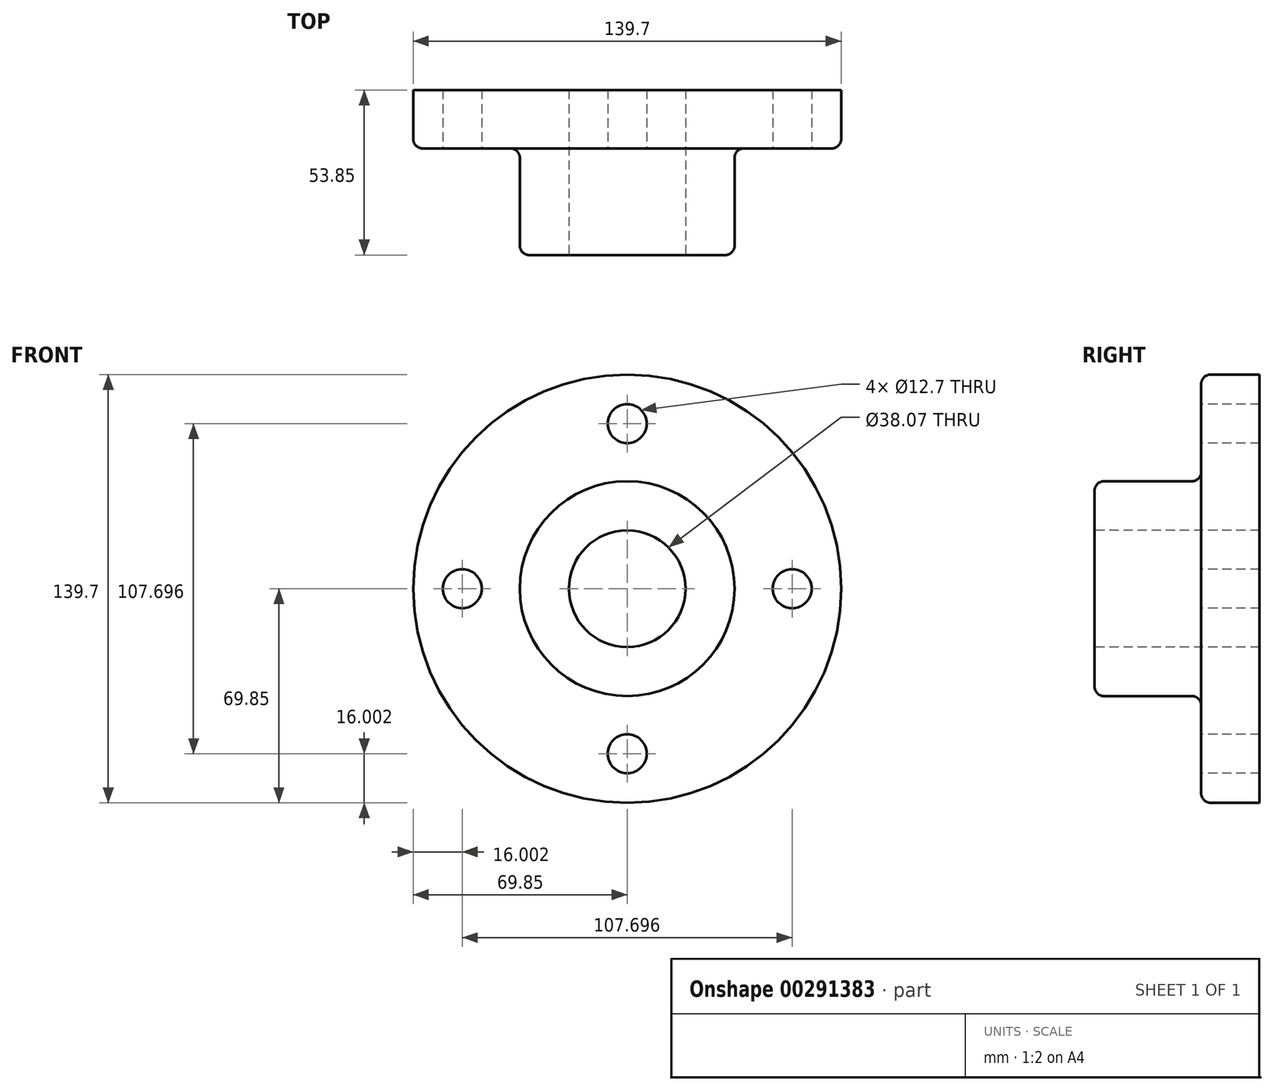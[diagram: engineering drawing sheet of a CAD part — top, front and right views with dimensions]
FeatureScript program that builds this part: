
annotation { "Feature Type Name" : "Feature", "Feature Type Description" : "" }
export const myFeature = defineFeature(function(context is Context, id is Id, definition is map)
    precondition{}
    {
        {
            var Q0;
            Q0=qCreatedBy(makeId("Right.planeOp"),FACE);
            var sketch = newSketch(context, id + "F0", { "sketchPlane" : qUnion([Q0])});
            skLineSegment(sketch, "E0", {"start": v(0, 0) * mm, "end": v(37.6, 0) * mm, "construction": true});
            skLineSegment(sketch, "E1", {"start": v(0, 19.04) * mm, "end": v(0, 32) * mm});
            skLineSegment(sketch, "E2", {"start": v(3.05, 35.05) * mm, "end": v(31.75, 35.05) * mm});
            skLineSegment(sketch, "E3", {"start": v(34.8, 38.1) * mm, "end": v(34.8, 66.8) * mm});
            skLineSegment(sketch, "E4", {"start": v(37.85, 69.85) * mm, "end": v(53.85, 69.85) * mm});
            skLineSegment(sketch, "E5", {"start": v(53.85, 69.85) * mm, "end": v(53.85, 19.04) * mm});
            skLineSegment(sketch, "E6", {"start": v(53.85, 19.04) * mm, "end": v(0, 19.04) * mm});
            skPoint(sketch, "E7.visualSharp", {"position": v(0, 35.05) * mm});
            skArc(sketch, "E7.filletArc", {"start": v(3.05, 35.05) * mm, "mid": v(0.9, 34.16) * mm, "end": v(0, 32) * mm});
            skPoint(sketch, "E8.visualSharp", {"position": v(34.8, 35.05) * mm});
            skArc(sketch, "E8.filletArc", {"start": v(31.75, 35.05) * mm, "mid": v(33.9, 35.94) * mm, "end": v(34.8, 38.1) * mm});
            skPoint(sketch, "E9.visualSharp", {"position": v(34.8, 69.85) * mm});
            skArc(sketch, "E9.filletArc", {"start": v(37.85, 69.85) * mm, "mid": v(35.7, 68.96) * mm, "end": v(34.8, 66.8) * mm});
            skSolve(sketch);
        }
        {
            var Q0;
            Q0=makeQuery(id+"F0.imprint","IMPRINT",FACE,{"disambiguationData":[TD([[makeQuery(id+"F0.imprint","IMPRINT",EDGE,{"derivedFrom":sQuery(id+"F0.wireOp",EDGE,"E1")}),-1.0]])]});
            var Q1;
            Q1=sQuery(id+"F0.wireOp",EDGE,"E0");
            revolve(context, id + "F1", {"entities" : qUnion([Q0]), "axis" : qUnion([Q1]), "revolveType" : RevolveType.FULL});
        }
        {
            var Q0;
            Q0=makeQuery(id+"F1.opRevolve","SWEPT_FACE",FACE,{"disambiguationData":[OSD([sQuery(id+"F0.wireOp",EDGE,"E3")])]});
            var sketch = newSketch(context, id + "F2", { "sketchPlane" : qUnion([Q0])});
            skCircle(sketch, "E10", {"center": v(0, 0) * mm, "radius": 53.85 * mm, "construction": true});
            skCircle(sketch, "E11", {"center": v(0, 53.85) * mm, "radius": 6.35 * mm});
            skCircle(sketch, "E12", {"center": v(-53.85, 0) * mm, "radius": 6.35 * mm});
            skCircle(sketch, "E13", {"center": v(0, -53.85) * mm, "radius": 6.35 * mm});
            skCircle(sketch, "E14", {"center": v(53.85, 0) * mm, "radius": 6.35 * mm});
            skSolve(sketch);
        }
        {
            var Q0;
            Q0=makeQuery(id+"F2.imprint","IMPRINT",FACE,{"disambiguationData":[TD([[makeQuery(id+"F2.imprint","IMPRINT",EDGE,{"derivedFrom":sQuery(id+"F2.wireOp",EDGE,"E12")}),1.0]])]});
            var Q1;
            Q1=makeQuery(id+"F2.imprint","IMPRINT",FACE,{"disambiguationData":[TD([[makeQuery(id+"F2.imprint","IMPRINT",EDGE,{"derivedFrom":sQuery(id+"F2.wireOp",EDGE,"E13")}),1.0]])]});
            var Q2;
            Q2=makeQuery(id+"F2.imprint","IMPRINT",FACE,{"disambiguationData":[TD([[makeQuery(id+"F2.imprint","IMPRINT",EDGE,{"derivedFrom":sQuery(id+"F2.wireOp",EDGE,"E11")}),1.0]])]});
            var Q3;
            Q3=makeQuery(id+"F2.imprint","IMPRINT",FACE,{"disambiguationData":[TD([[makeQuery(id+"F2.imprint","IMPRINT",EDGE,{"derivedFrom":sQuery(id+"F2.wireOp",EDGE,"E14")}),1.0]])]});
            extrude(context, id + "F3", {"entities" : qUnion([Q0, Q1, Q2, Q3]), "operationType" : NewBodyOperationType.REMOVE, "endBound" : BoundingType.THROUGH_ALL, "oppositeDirection" : true, "depth" : 25.4 * mm});
        }
    });
